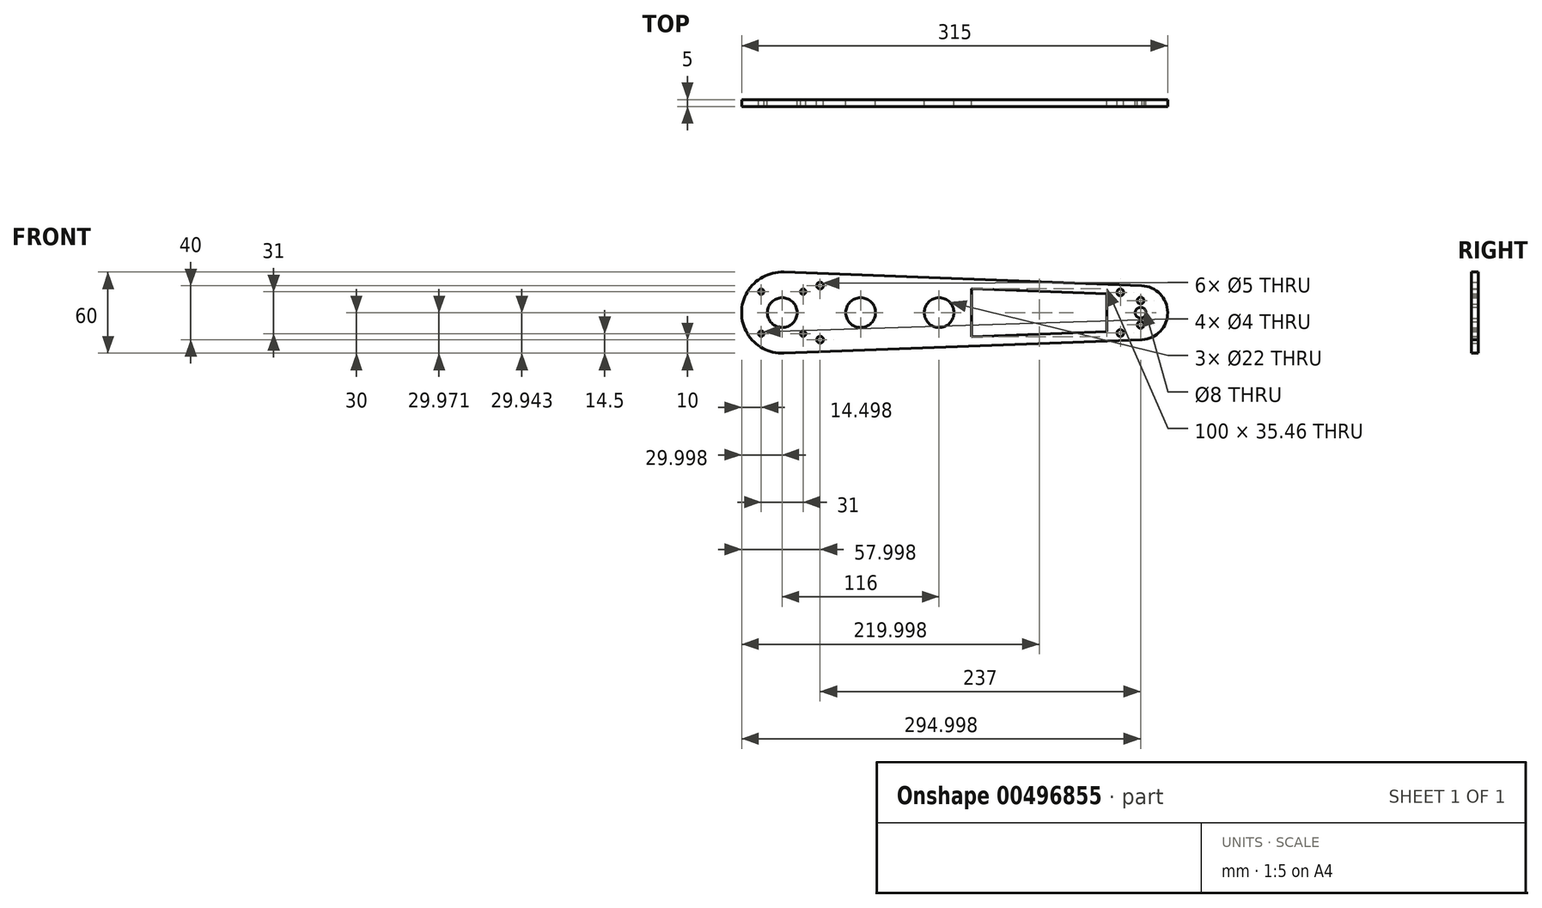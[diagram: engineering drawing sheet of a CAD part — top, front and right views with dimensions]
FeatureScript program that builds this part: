
annotation { "Feature Type Name" : "Feature", "Feature Type Description" : "" }
export const myFeature = defineFeature(function(context is Context, id is Id, definition is map)
    precondition{}
    {
        {
            var Q0;
            Q0=qCreatedBy(makeId("Front.planeOp"),FACE);
            var sketch = newSketch(context, id + "F0", { "sketchPlane" : qUnion([Q0])});
            skArc(sketch, "E0", {"start": v(-80.16, 29.98) * mm, "mid": v(-111.3, 0) * mm, "end": v(-80.18, -29.98) * mm});
            skCircle(sketch, "E1", {"center": v(-81.3, 0) * mm, "radius": 11 * mm});
            skLineSegment(sketch, "E2", {"start": v(-80.18, -29.98) * mm, "end": v(184.76, -20.03) * mm});
            skLineSegment(sketch, "E3", {"start": v(-80.16, 29.98) * mm, "end": v(184.46, 19.93) * mm});
            skCircle(sketch, "E4", {"center": v(-23.3, 0) * mm, "radius": 11 * mm});
            skCircle(sketch, "E5", {"center": v(34.7, 0) * mm, "radius": 11 * mm});
            skCircle(sketch, "E6", {"center": v(-96.8, 15.5) * mm, "radius": 2 * mm});
            skCircle(sketch, "E7", {"center": v(-65.8, 15.5) * mm, "radius": 2 * mm});
            skCircle(sketch, "E8", {"center": v(-65.8, -15.5) * mm, "radius": 2 * mm});
            skCircle(sketch, "E9", {"center": v(-96.8, -15.5) * mm, "radius": 2 * mm});
            skCircle(sketch, "E10", {"center": v(168.7, 15) * mm, "radius": 2.5 * mm});
            skCircle(sketch, "E11", {"center": v(168.7, -15) * mm, "radius": 2.5 * mm});
            skCircle(sketch, "E12", {"center": v(-53.3, 20) * mm, "radius": 2.5 * mm});
            skCircle(sketch, "E13", {"center": v(-53.3, -20) * mm, "radius": 2.5 * mm});
            skArc(sketch, "E14", {"start": v(184.46, 19.93) * mm, "mid": v(203.7, 0.1) * mm, "end": v(184.76, -20.03) * mm});
            skCircle(sketch, "E15", {"center": v(183.7, -0.06) * mm, "radius": 4 * mm});
            skLineSegment(sketch, "E16", {"start": v(183.7, -0.06) * mm, "end": v(183.7, 8.94) * mm});
            skLineSegment(sketch, "E17", {"start": v(183.7, -0.06) * mm, "end": v(183.7, -9.06) * mm});
            skCircle(sketch, "E18", {"center": v(183.7, 8.94) * mm, "radius": 2.5 * mm});
            skCircle(sketch, "E19", {"center": v(183.7, -9.06) * mm, "radius": 2.5 * mm});
            skLineSegment(sketch, "E20", {"start": v(58.7, 17.7) * mm, "end": v(158.7, 13.9) * mm});
            skLineSegment(sketch, "E21", {"start": v(58.7, -17.76) * mm, "end": v(158.7, -14) * mm});
            skLineSegment(sketch, "E22", {"start": v(158.7, -14) * mm, "end": v(158.7, 13.9) * mm});
            skLineSegment(sketch, "E23", {"start": v(58.7, 17.7) * mm, "end": v(58.7, -17.76) * mm});
            skSolve(sketch);
        }
        {
            var Q0;
            Q0 = qSketchRegion(id + "F0", true);
            extrude(context, id + "F1", {"entities" : qUnion([Q0]), "depth" : 5 * mm});
        }
    });
